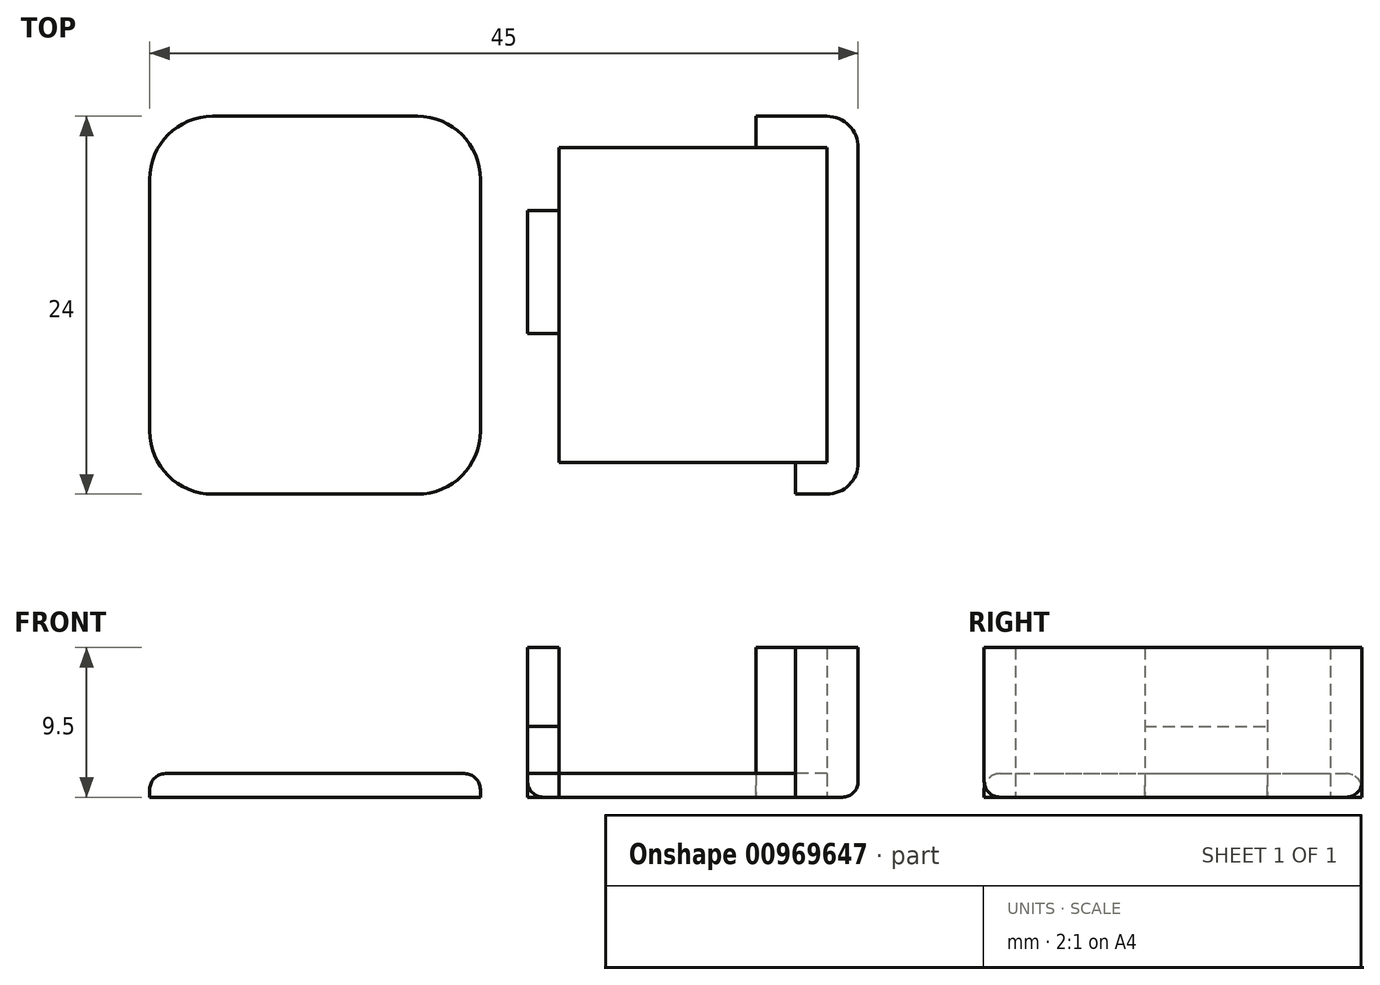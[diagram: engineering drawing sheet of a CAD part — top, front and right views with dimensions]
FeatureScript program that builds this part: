
annotation { "Feature Type Name" : "Feature", "Feature Type Description" : "" }
export const myFeature = defineFeature(function(context is Context, id is Id, definition is map)
    precondition{}
    {
        {
            var Q0;
            Q0=qCreatedBy(makeId("Top.planeOp"),FACE);
            var sketch = newSketch(context, id + "F0", { "sketchPlane" : qUnion([Q0])});
            skLineSegment(sketch, "E0.bottom", {"start": v(8.5, -10) * mm, "end": v(-8.5, -10) * mm});
            skLineSegment(sketch, "E0.top", {"start": v(8.5, 10) * mm, "end": v(-8.5, 10) * mm});
            skLineSegment(sketch, "E0.left", {"start": v(8.5, -10) * mm, "end": v(8.5, 10) * mm});
            skLineSegment(sketch, "E0.right", {"start": v(-8.5, -10) * mm, "end": v(-8.5, 10) * mm});
            skPoint(sketch, "E0.middle", {"position": v(0, 0) * mm});
            skLineSegment(sketch, "E1.0", {"start": v(10.5, -10) * mm, "end": v(10.5, 10) * mm});
            skLineSegment(sketch, "E1.1", {"start": v(8.5, -12) * mm, "end": v(-8.5, -12) * mm});
            skLineSegment(sketch, "E1.2", {"start": v(-10.5, -10) * mm, "end": v(-10.5, 10) * mm});
            skLineSegment(sketch, "E1.3", {"start": v(8.5, 12) * mm, "end": v(-8.5, 12) * mm});
            skLineSegment(sketch, "E2.bottom", {"start": v(-4, 12) * mm, "end": v(4, 12) * mm});
            skLineSegment(sketch, "E2.top", {"start": v(-4, 10) * mm, "end": v(4, 10) * mm});
            skLineSegment(sketch, "E2.left", {"start": v(-4, 12) * mm, "end": v(-4, 10) * mm});
            skLineSegment(sketch, "E2.right", {"start": v(4, 12) * mm, "end": v(4, 10) * mm});
            skPoint(sketch, "E3.visualSharp", {"position": v(-10.5, 12) * mm});
            skArc(sketch, "E3.filletArc", {"start": v(-8.5, 12) * mm, "mid": v(-9.91, 11.41) * mm, "end": v(-10.5, 10) * mm});
            skPoint(sketch, "E4.visualSharp", {"position": v(10.5, 12) * mm});
            skArc(sketch, "E4.filletArc", {"start": v(10.5, 10) * mm, "mid": v(9.91, 11.41) * mm, "end": v(8.5, 12) * mm});
            skPoint(sketch, "E5.visualSharp", {"position": v(10.5, -12) * mm});
            skArc(sketch, "E5.filletArc", {"start": v(8.5, -12) * mm, "mid": v(9.91, -11.41) * mm, "end": v(10.5, -10) * mm});
            skPoint(sketch, "E6.visualSharp", {"position": v(-10.5, -12) * mm});
            skArc(sketch, "E6.filletArc", {"start": v(-10.5, -10) * mm, "mid": v(-9.91, -11.41) * mm, "end": v(-8.5, -12) * mm});
            skLineSegment(sketch, "E7.bottom", {"start": v(-6.5, -10) * mm, "end": v(6.5, -10) * mm});
            skLineSegment(sketch, "E7.top", {"start": v(-6.5, -12) * mm, "end": v(6.5, -12) * mm});
            skLineSegment(sketch, "E7.left", {"start": v(-6.5, -10) * mm, "end": v(-6.5, -12) * mm});
            skLineSegment(sketch, "E7.right", {"start": v(6.5, -10) * mm, "end": v(6.5, -12) * mm});
            skLineSegment(sketch, "E8.bottom", {"start": v(-10.5, 6) * mm, "end": v(-8.5, 6) * mm});
            skLineSegment(sketch, "E8.top", {"start": v(-10.5, -1.8) * mm, "end": v(-8.5, -1.8) * mm});
            skLineSegment(sketch, "E8.left", {"start": v(-10.5, 6) * mm, "end": v(-10.5, -1.8) * mm});
            skLineSegment(sketch, "E8.right", {"start": v(-8.5, 6) * mm, "end": v(-8.5, -1.8) * mm});
            skSolve(sketch);
        }
        {
            var Q0;
            {var subQ1=sQuery(id+"F0.wireOp",EDGE,"E0.left");Q0=makeQuery(id+"F0.imprint","IMPRINT",FACE,{"disambiguationData":[TD([[makeQuery(id+"F0.imprint","IMPRINT",EDGE,{"derivedFrom":subQ1}),-1.0]])]});}
            var Q1;
            {var subQ0=sQuery(id+"F0.wireOp",EDGE,"E0.right");Q1=makeQuery(id+"F0.imprint","IMPRINT",FACE,{"disambiguationData":[TD([[makeQuery(id+"F0.imprint","IMPRINT",EDGE,{"derivedFrom":subQ0}),1.0]])]});}
            extrude(context, id + "F1", {"entities" : qUnion([Q0, Q1]), "depth" : 9.5 * mm, "offsetDistance" : 25 * mm});
        }
        {
            var Q0;
            Q0=qCreatedBy(makeId("Top.planeOp"),FACE);
            var sketch = newSketch(context, id + "F2", { "sketchPlane" : qUnion([Q0])});
            skLineSegment(sketch, "E9.bottom", {"start": v(8.5, -10) * mm, "end": v(-8.5, -10) * mm});
            skLineSegment(sketch, "E9.top", {"start": v(8.5, 10) * mm, "end": v(-8.5, 10) * mm});
            skLineSegment(sketch, "E9.left", {"start": v(8.5, -10) * mm, "end": v(8.5, 10) * mm});
            skLineSegment(sketch, "E9.right", {"start": v(-8.5, -10) * mm, "end": v(-8.5, 10) * mm});
            skPoint(sketch, "E9.middle", {"position": v(0, 0) * mm});
            skLineSegment(sketch, "E10.0", {"start": v(10.5, -10) * mm, "end": v(10.5, 10) * mm});
            skLineSegment(sketch, "E10.1", {"start": v(8.5, -12) * mm, "end": v(-8.5, -12) * mm});
            skLineSegment(sketch, "E10.2", {"start": v(-10.5, -10) * mm, "end": v(-10.5, 10) * mm});
            skLineSegment(sketch, "E10.3", {"start": v(8.5, 12) * mm, "end": v(-8.5, 12) * mm});
            skLineSegment(sketch, "E11.bottom", {"start": v(-4, 12) * mm, "end": v(4, 12) * mm});
            skLineSegment(sketch, "E11.top", {"start": v(-4, 10) * mm, "end": v(4, 10) * mm});
            skLineSegment(sketch, "E11.left", {"start": v(-4, 12) * mm, "end": v(-4, 10) * mm});
            skLineSegment(sketch, "E11.right", {"start": v(4, 12) * mm, "end": v(4, 10) * mm});
            skPoint(sketch, "E12.visualSharp", {"position": v(-10.5, 12) * mm});
            skArc(sketch, "E12.filletArc", {"start": v(-8.5, 12) * mm, "mid": v(-9.91, 11.41) * mm, "end": v(-10.5, 10) * mm});
            skPoint(sketch, "E13.visualSharp", {"position": v(10.5, 12) * mm});
            skArc(sketch, "E13.filletArc", {"start": v(10.5, 10) * mm, "mid": v(9.91, 11.41) * mm, "end": v(8.5, 12) * mm});
            skPoint(sketch, "E14.visualSharp", {"position": v(10.5, -12) * mm});
            skArc(sketch, "E14.filletArc", {"start": v(8.5, -12) * mm, "mid": v(9.91, -11.41) * mm, "end": v(10.5, -10) * mm});
            skPoint(sketch, "E15.visualSharp", {"position": v(-10.5, -12) * mm});
            skArc(sketch, "E15.filletArc", {"start": v(-10.5, -10) * mm, "mid": v(-9.91, -11.41) * mm, "end": v(-8.5, -12) * mm});
            skLineSegment(sketch, "E16.bottom", {"start": v(-6.5, -10) * mm, "end": v(6.5, -10) * mm});
            skLineSegment(sketch, "E16.top", {"start": v(-6.5, -12) * mm, "end": v(6.5, -12) * mm});
            skLineSegment(sketch, "E16.left", {"start": v(-6.5, -10) * mm, "end": v(-6.5, -12) * mm});
            skLineSegment(sketch, "E16.right", {"start": v(6.5, -10) * mm, "end": v(6.5, -12) * mm});
            skLineSegment(sketch, "E17.bottom", {"start": v(-10.5, 6) * mm, "end": v(-8.5, 6) * mm});
            skLineSegment(sketch, "E17.top", {"start": v(-10.5, -1.8) * mm, "end": v(-8.5, -1.8) * mm});
            skLineSegment(sketch, "E17.left", {"start": v(-10.5, 6) * mm, "end": v(-10.5, -1.8) * mm});
            skLineSegment(sketch, "E17.right", {"start": v(-8.5, 6) * mm, "end": v(-8.5, -1.8) * mm});
            skSolve(sketch);
        }
        {
            var Q0;
            {var subQ4=sQuery(id+"F2.wireOp",EDGE,"E9.left");Q0=makeQuery(id+"F2.imprint","IMPRINT",FACE,{"disambiguationData":[TD([[makeQuery(id+"F2.imprint","IMPRINT",EDGE,{"derivedFrom":subQ4}),1.0]])]});}
            var Q1;
            Q1=makeQuery(id+"F2.imprint","IMPRINT",FACE,{"disambiguationData":[TD([[makeQuery(id+"F2.imprint","IMPRINT",EDGE,{"derivedFrom":sQuery(id+"F2.wireOp",EDGE,"E11.bottom")}),-1.0]])]});
            var Q2;
            Q2=makeQuery(id+"F2.imprint","IMPRINT",FACE,{"disambiguationData":[TD([[makeQuery(id+"F2.imprint","IMPRINT",EDGE,{"derivedFrom":sQuery(id+"F2.wireOp",EDGE,"E17.bottom")}),-1.0]])]});
            var Q3;
            Q3=makeQuery(id+"F2.imprint","IMPRINT",FACE,{"disambiguationData":[TD([[makeQuery(id+"F2.imprint","IMPRINT",EDGE,{"derivedFrom":sQuery(id+"F2.wireOp",EDGE,"E16.bottom")}),-1.0]])]});
            extrude(context, id + "F3", {"entities" : qUnion([Q0, Q1, Q2, Q3]), "depth" : 1.5 * mm, "offsetDistance" : 25 * mm});
        }
        {
            var Q0;
            Q0=qCreatedBy(makeId("Top.planeOp"),FACE);
            var sketch = newSketch(context, id + "F4", { "sketchPlane" : qUnion([Q0])});
            skLineSegment(sketch, "E18.bottom", {"start": v(8.5, -10) * mm, "end": v(-8.5, -10) * mm});
            skLineSegment(sketch, "E18.top", {"start": v(8.5, 10) * mm, "end": v(-8.5, 10) * mm});
            skLineSegment(sketch, "E18.left", {"start": v(8.5, -10) * mm, "end": v(8.5, 10) * mm});
            skLineSegment(sketch, "E18.right", {"start": v(-8.5, -10) * mm, "end": v(-8.5, 10) * mm});
            skPoint(sketch, "E18.middle", {"position": v(0, 0) * mm});
            skLineSegment(sketch, "E19.0", {"start": v(10.5, -10) * mm, "end": v(10.5, 10) * mm});
            skLineSegment(sketch, "E19.1", {"start": v(8.5, -12) * mm, "end": v(-8.5, -12) * mm});
            skLineSegment(sketch, "E19.2", {"start": v(-10.5, -10) * mm, "end": v(-10.5, 10) * mm});
            skLineSegment(sketch, "E19.3", {"start": v(8.5, 12) * mm, "end": v(-8.5, 12) * mm});
            skLineSegment(sketch, "E20.bottom", {"start": v(-4, 12) * mm, "end": v(4, 12) * mm});
            skLineSegment(sketch, "E20.top", {"start": v(-4, 10) * mm, "end": v(4, 10) * mm});
            skLineSegment(sketch, "E20.left", {"start": v(-4, 12) * mm, "end": v(-4, 10) * mm});
            skLineSegment(sketch, "E20.right", {"start": v(4, 12) * mm, "end": v(4, 10) * mm});
            skPoint(sketch, "E21.visualSharp", {"position": v(-10.5, 12) * mm});
            skArc(sketch, "E21.filletArc", {"start": v(-8.5, 12) * mm, "mid": v(-9.91, 11.41) * mm, "end": v(-10.5, 10) * mm});
            skPoint(sketch, "E22.visualSharp", {"position": v(10.5, 12) * mm});
            skArc(sketch, "E22.filletArc", {"start": v(10.5, 10) * mm, "mid": v(9.91, 11.41) * mm, "end": v(8.5, 12) * mm});
            skPoint(sketch, "E23.visualSharp", {"position": v(10.5, -12) * mm});
            skArc(sketch, "E23.filletArc", {"start": v(8.5, -12) * mm, "mid": v(9.91, -11.41) * mm, "end": v(10.5, -10) * mm});
            skPoint(sketch, "E24.visualSharp", {"position": v(-10.5, -12) * mm});
            skArc(sketch, "E24.filletArc", {"start": v(-10.5, -10) * mm, "mid": v(-9.91, -11.41) * mm, "end": v(-8.5, -12) * mm});
            skLineSegment(sketch, "E25.bottom", {"start": v(-6.5, -10) * mm, "end": v(6.5, -10) * mm});
            skLineSegment(sketch, "E25.top", {"start": v(-6.5, -12) * mm, "end": v(6.5, -12) * mm});
            skLineSegment(sketch, "E25.left", {"start": v(-6.5, -10) * mm, "end": v(-6.5, -12) * mm});
            skLineSegment(sketch, "E25.right", {"start": v(6.5, -10) * mm, "end": v(6.5, -12) * mm});
            skLineSegment(sketch, "E26.bottom", {"start": v(-10.5, 6) * mm, "end": v(-8.5, 6) * mm});
            skLineSegment(sketch, "E26.top", {"start": v(-10.5, -1.8) * mm, "end": v(-8.5, -1.8) * mm});
            skLineSegment(sketch, "E26.left", {"start": v(-10.5, 6) * mm, "end": v(-10.5, -1.8) * mm});
            skLineSegment(sketch, "E26.right", {"start": v(-8.5, 6) * mm, "end": v(-8.5, -1.8) * mm});
            skSolve(sketch);
        }
        {
            var Q0;
            Q0=makeQuery(id+"F4.imprint","IMPRINT",FACE,{"disambiguationData":[TD([[makeQuery(id+"F4.imprint","IMPRINT",EDGE,{"derivedFrom":sQuery(id+"F4.wireOp",EDGE,"E20.bottom")}),-1.0]])]});
            var Q1;
            Q1=makeQuery(id+"F4.imprint","IMPRINT",FACE,{"disambiguationData":[TD([[makeQuery(id+"F4.imprint","IMPRINT",EDGE,{"derivedFrom":sQuery(id+"F4.wireOp",EDGE,"E26.bottom")}),-1.0]])]});
            var Q2;
            Q2=makeQuery(id+"F4.imprint","IMPRINT",FACE,{"disambiguationData":[TD([[makeQuery(id+"F4.imprint","IMPRINT",EDGE,{"derivedFrom":sQuery(id+"F4.wireOp",EDGE,"E25.bottom")}),-1.0]])]});
            extrude(context, id + "F5", {"entities" : qUnion([Q0, Q1, Q2]), "depth" : 9.5 * mm, "offsetDistance" : 25 * mm, "hasSecondDirection" : true, "secondDirectionOppositeDirection" : false, "secondDirectionDepth" : 4.5 * mm});
        }
        {
            var Q0;
            Q0=makeQuery(id+"F1.opExtrude","CAP_EDGE",EDGE,{"disambiguationData":[OSD([sQuery(id+"F0.wireOp",EDGE,"E4.filletArc")])],"isStart":true});
            var Q1;
            Q1=makeQuery(id+"F3.opExtrude","CAP_EDGE",EDGE,{"disambiguationData":[OSD([sQuery(id+"F2.wireOp",EDGE,"E11.bottom")])],"isStart":true});
            var Q2;
            Q2=makeQuery(id+"F1.opExtrude","CAP_EDGE",EDGE,{"disambiguationData":[OSD([sQuery(id+"F0.wireOp",EDGE,"E3.filletArc")])],"isStart":true});
            var Q3;
            Q3=makeQuery(id+"F3.opExtrude","CAP_EDGE",EDGE,{"disambiguationData":[OSD([sQuery(id+"F2.wireOp",EDGE,"E17.left")])],"isStart":true});
            var Q4;
            {var subQ0=sQuery(id+"F0.wireOp",EDGE,"E1.2");Q4=makeQuery(id+"F1.opExtrude","CAP_EDGE",EDGE,{"disambiguationData":[OSD([subQ0]),TDD([makeQuery(id+"F0.imprint","IMPRINT",EDGE,{"disambiguationData":[TD([[makeQuery(id+"F0.imprint","INTERSECT",VERTEX,{"derivedFrom":[subQ0,sQuery(id+"F0.wireOp",EDGE,"E6.filletArc")]}),-1.0]])],"derivedFrom":subQ0})])],"isStart":true});}
            var Q5;
            Q5=makeQuery(id+"F3.opExtrude","CAP_EDGE",EDGE,{"disambiguationData":[OSD([sQuery(id+"F2.wireOp",EDGE,"E16.top")])],"isStart":true});
            fillet(context, id + "F6", {"entities" : qUnion([Q0, Q1, Q2, Q3, Q4, Q5]), "radius" : 1 * mm, "tangentPropagation" : true, "allowEdgeOverflow" : false});
        }
        {
            var Q0;
            Q0=qCreatedBy(makeId("Top.planeOp"),FACE);
            var sketch = newSketch(context, id + "F7", { "sketchPlane" : qUnion([Q0])});
            skLineSegment(sketch, "E27.bottom", {"start": v(-17.5, -10) * mm, "end": v(-30.5, -10) * mm});
            skLineSegment(sketch, "E27.top", {"start": v(-17.5, 10) * mm, "end": v(-30.5, 10) * mm});
            skLineSegment(sketch, "E27.left", {"start": v(-15.5, -8) * mm, "end": v(-15.5, 8) * mm});
            skLineSegment(sketch, "E27.right", {"start": v(-32.5, -8) * mm, "end": v(-32.5, 8) * mm});
            skPoint(sketch, "E27.middle", {"position": v(-24, 0) * mm});
            skPoint(sketch, "E28.visualSharp", {"position": v(-32.5, 10) * mm});
            skArc(sketch, "E28.filletArc", {"start": v(-30.5, 10) * mm, "mid": v(-31.91, 9.41) * mm, "end": v(-32.5, 8) * mm});
            skPoint(sketch, "E29.visualSharp", {"position": v(-15.5, 10) * mm});
            skArc(sketch, "E29.filletArc", {"start": v(-15.5, 8) * mm, "mid": v(-16.09, 9.41) * mm, "end": v(-17.5, 10) * mm});
            skPoint(sketch, "E30.visualSharp", {"position": v(-15.5, -10) * mm});
            skArc(sketch, "E30.filletArc", {"start": v(-17.5, -10) * mm, "mid": v(-16.09, -9.41) * mm, "end": v(-15.5, -8) * mm});
            skPoint(sketch, "E31.visualSharp", {"position": v(-32.5, -10) * mm});
            skArc(sketch, "E31.filletArc", {"start": v(-32.5, -8) * mm, "mid": v(-31.91, -9.41) * mm, "end": v(-30.5, -10) * mm});
            skArc(sketch, "E32.0", {"start": v(-13.5, 8) * mm, "mid": v(-14.67, 10.83) * mm, "end": v(-17.5, 12) * mm});
            skLineSegment(sketch, "E32.1", {"start": v(-13.5, -8) * mm, "end": v(-13.5, 8) * mm});
            skLineSegment(sketch, "E32.2", {"start": v(-17.5, 12) * mm, "end": v(-30.5, 12) * mm});
            skArc(sketch, "E32.3", {"start": v(-17.5, -12) * mm, "mid": v(-14.67, -10.83) * mm, "end": v(-13.5, -8) * mm});
            skArc(sketch, "E32.4", {"start": v(-30.5, 12) * mm, "mid": v(-33.33, 10.83) * mm, "end": v(-34.5, 8) * mm});
            skLineSegment(sketch, "E32.5", {"start": v(-34.5, -8) * mm, "end": v(-34.5, 8) * mm});
            skArc(sketch, "E32.6", {"start": v(-34.5, -8) * mm, "mid": v(-33.33, -10.83) * mm, "end": v(-30.5, -12) * mm});
            skLineSegment(sketch, "E32.7", {"start": v(-17.5, -12) * mm, "end": v(-30.5, -12) * mm});
            skSolve(sketch);
        }
        {
            var Q0;
            Q0=makeQuery(id+"F7.imprint","IMPRINT",FACE,{"disambiguationData":[TD([[makeQuery(id+"F7.imprint","IMPRINT",EDGE,{"derivedFrom":sQuery(id+"F7.wireOp",EDGE,"E27.bottom")}),-1.0]])]});
            var Q1;
            Q1=makeQuery(id+"F7.imprint","IMPRINT",FACE,{"disambiguationData":[TD([[makeQuery(id+"F7.imprint","IMPRINT",EDGE,{"derivedFrom":sQuery(id+"F7.wireOp",EDGE,"E27.bottom")}),1.0]])]});
            extrude(context, id + "F8", {"entities" : qUnion([Q0, Q1]), "depth" : 1.5 * mm, "offsetDistance" : 25 * mm});
        }
        {
            var Q0;
            Q0=makeQuery(id+"F8.opExtrude","CAP_FACE",FACE,{"disambiguationData":[OSD([sQuery(id+"F7.wireOp",EDGE,"E32.0"),sQuery(id+"F7.wireOp",EDGE,"E32.1"),sQuery(id+"F7.wireOp",EDGE,"E32.2"),sQuery(id+"F7.wireOp",EDGE,"E32.3"),sQuery(id+"F7.wireOp",EDGE,"E32.4"),sQuery(id+"F7.wireOp",EDGE,"E32.5"),sQuery(id+"F7.wireOp",EDGE,"E32.6"),sQuery(id+"F7.wireOp",EDGE,"E32.7")])],"isStart":false});
            fillet(context, id + "F9", {"entities" : qUnion([Q0]), "radius" : 1 * mm, "tangentPropagation" : true, "allowEdgeOverflow" : false});
        }
    });
